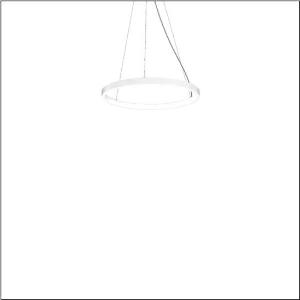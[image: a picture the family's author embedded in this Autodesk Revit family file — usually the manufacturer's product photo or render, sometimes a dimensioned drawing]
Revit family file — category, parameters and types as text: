
# Revit family: silica_r__21_ring-i_5pjbi1d3004a_1a46
name_source: partatom
category: Lighting Fixtures
units: mm (PartAtom-declared; Revit-internal decimal feet)

## family parameters
Cut with Voids When Loaded = No
Host = Face
Light Source = No
Part Type = Normal
Room Calculation Point = No
Round Connector Dimension = Use Diameter
Shared = No

## types (1)
- Silica® 21 Ring-I (1 x LED, 3510 lm, 60 W, 4000K)
    Apparent Load = 60 VA
    CIE Flux Codes = 22 48 76 50 101
    Color Rendering = 80
    Color Temperature = 4000K
    Default Elevation = 1800 mm
    Description = Silica® 21 Ring-I, suspended luminaire, of PMMA, frosted, light emission: inner ring side luminous distribution, primary light characteristic: symmetric, installation type: suspended mounting, LED, rated luminous flux: 3.510lm, luminous efficacy: 59lm/W, light colour: 840, colour temperature: 4000K, with terminal, 5-pole, mains connection: 230V, AC/DC, 0/50..60Hz, rated input power: 60W, housing, of extruded aluminium section, traffic white (RAL 9016), diameter: 610mm, ceiling canopy, traffic white (RAL 9016), protection rating (lamp compartment): IP40, insulation class (complete): insulation class I (protective earthing), certification: CE, impact resistance: IK02, permissible operating ambient temperature: 0..+35°C, packaging unit: 1 piece
    Height = 48 mm  [stored 0.15748 ft]
    Lamp = 1 x LED
    Lamp Light Flux = 3510 lm
    Lamp Power = 60 W
    Lamp count = 1
    Length = 610 mm
    Luminous efficacy = 59 lm/W
    Manufacturer = Siteco
    ModVariant = No
    Model = 5PJBI1D3004A
    Mounting Place = Ceiling
    Mounting Type = Pendant
    Number of Poles = 1
    OnlyDefault = Yes
    Power Factor = 1
    Product Name = Silica® 21 Ring-I
    Product group = suspended luminaire
    ProductGroupID = 904
    Protection Class = Protection class I
    Protection Degree = Degree of protection
    RLX_Detail_Level = 1
    RLX_Emergency_Light_Flux = 0 lm
    RLX_Emergency_Type = 0
    RLX_Emergency_Type_DB = No
    RlxData = <blob elided: 10469 chars, md5=37afb31e>
    Socket = socket
    Standby Power = 0 W
    System Light Flux = 3510 lm
    System Power = 60 W
    Type Comments = Product without accessories
    Type Image = l_1258363.jpg
    URL = http://relux.com
    VarID = ---
    Voltage = 0 V
    Weight = 0.00 kg
    Width = 0 mm  [stored 0 ft]

note: [stored X ft] marks values corroborated as IEEE doubles in the binary element streams (Revit-internal decimal feet)

## geometry (parser evidence)
native form markers: Sweep x15
no freeform markers — native parametric forms only
